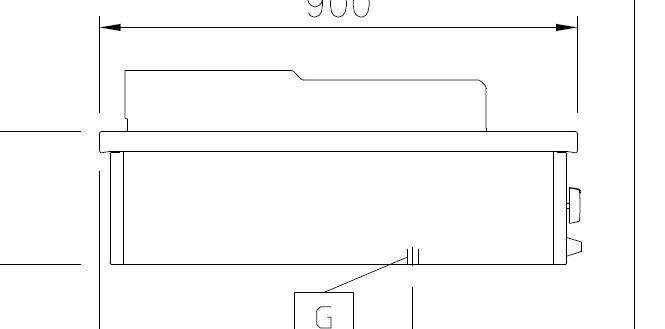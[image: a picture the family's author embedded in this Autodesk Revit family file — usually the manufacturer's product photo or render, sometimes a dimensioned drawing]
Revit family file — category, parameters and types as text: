
# Revit family: QF_ELECTROLUXPROFESSIONAL_589281_MCDBABHOPO
name_source: partatom
category: Specialty Equipment
revit_build: Autodesk Revit 2018 (Build: 20190510_1515(x64)
units: mm (PartAtom-declared; Revit-internal decimal feet)

## family parameters
Always vertical = Yes
Cut with Voids When Loaded = No
Part Type = Normal
Room Calculation Point = No
Round Connector Dimension = Use Diameter
Shared = No
Work Plane-Based = No

## types (1)
- QF_ELECTROLUXPROFESSIONAL_589281_MCDBABHOPO
    Description = GAS CHARGRILL,1SIDE,BACKSPL,800X900X250H
    Direct Waste Size = 0"
    Gas Connection Height = 0 mm  [stored 0 ft]
    Gas KW = 21
    Gas Size = 1"
    HP = 0 HP
    Manufacturer = ELECTROLUX
    Model = 589281
    Watts = 0 W
    Weight in Pounds = 253.5

note: [stored X ft] marks values corroborated as IEEE doubles in the binary element streams (Revit-internal decimal feet)

## geometry (parser evidence)
native form markers: Blend x27, Sweep x13
no freeform markers — native parametric forms only
